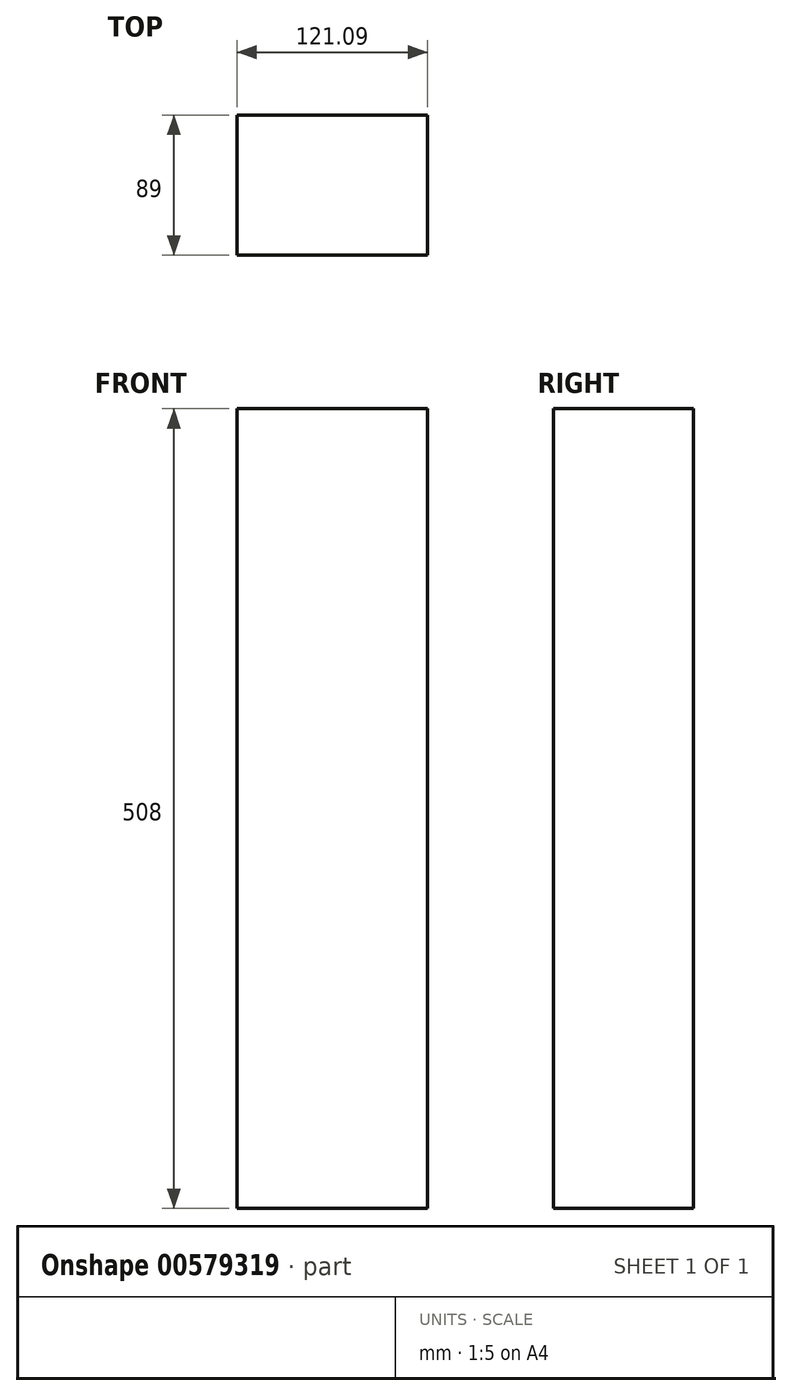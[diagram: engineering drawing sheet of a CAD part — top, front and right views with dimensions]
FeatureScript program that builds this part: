
annotation { "Feature Type Name" : "Feature", "Feature Type Description" : "" }
export const myFeature = defineFeature(function(context is Context, id is Id, definition is map)
    precondition{}
    {
        {
            var Q0;
            Q0=qCreatedBy(makeId("Top.planeOp"),FACE);
            var sketch = newSketch(context, id + "F0", { "sketchPlane" : qUnion([Q0])});
            skLineSegment(sketch, "E0.bottom", {"start": v(-62.47, 50.92) * mm, "end": v(58.62, 50.92) * mm});
            skLineSegment(sketch, "E0.top", {"start": v(-62.47, -38.08) * mm, "end": v(58.62, -38.08) * mm});
            skLineSegment(sketch, "E0.left", {"start": v(-62.47, 50.92) * mm, "end": v(-62.47, -38.08) * mm});
            skLineSegment(sketch, "E0.right", {"start": v(58.62, 50.92) * mm, "end": v(58.62, -38.08) * mm});
            skSolve(sketch);
        }
        {
            var Q0;
            Q0=makeQuery(id+"F0.imprint","IMPRINT",FACE,{"disambiguationData":[TD([[makeQuery(id+"F0.imprint","IMPRINT",EDGE,{"derivedFrom":sQuery(id+"F0.wireOp",EDGE,"E0.bottom")}),-1.0]])]});
            extrude(context, id + "F1", {"entities" : qUnion([Q0]), "depth" : 508 * mm, "offsetDistance" : 25.4 * mm});
        }
    });
